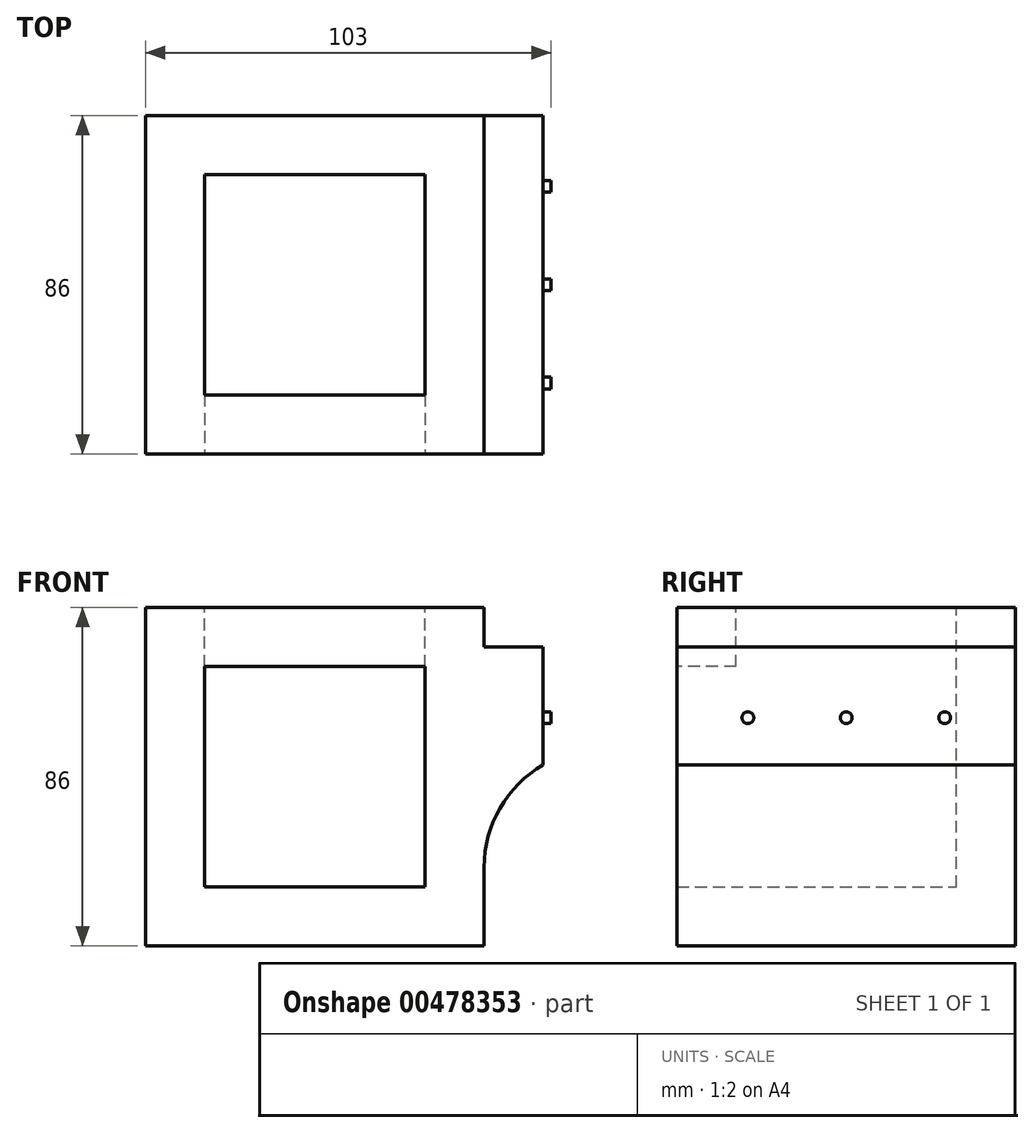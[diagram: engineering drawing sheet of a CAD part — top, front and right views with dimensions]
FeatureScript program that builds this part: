
annotation { "Feature Type Name" : "Feature", "Feature Type Description" : "" }
export const myFeature = defineFeature(function(context is Context, id is Id, definition is map)
    precondition{}
    {
        {
            var Q0;
            Q0=qCreatedBy(makeId("Top.planeOp"),FACE);
            var sketch = newSketch(context, id + "F0", { "sketchPlane" : qUnion([Q0])});
            skLineSegment(sketch, "E0", {"start": v(0, 0) * mm, "end": v(-43, 0) * mm});
            skLineSegment(sketch, "E1", {"start": v(-43, 0) * mm, "end": v(-43, 43) * mm});
            skLineSegment(sketch, "E2", {"start": v(-43, 43) * mm, "end": v(0, 43) * mm});
            skLineSegment(sketch, "E3", {"start": v(0, 43) * mm, "end": v(0, 0) * mm});
            skLineSegment(sketch, "E4.MirrorCS", {"start": v(43, 0) * mm, "end": v(43, 43) * mm});
            skLineSegment(sketch, "E5.MirrorCS", {"start": v(43, 43) * mm, "end": v(0, 43) * mm});
            skLineSegment(sketch, "E6.MirrorCS", {"start": v(43, -43) * mm, "end": v(0, -43) * mm});
            skLineSegment(sketch, "E7.MirrorCS", {"start": v(-43, -43) * mm, "end": v(0, -43) * mm});
            skLineSegment(sketch, "E8.MirrorCS", {"start": v(-43, 0) * mm, "end": v(-43, -43) * mm});
            skLineSegment(sketch, "E9.MirrorCS", {"start": v(43, 0) * mm, "end": v(43, -43) * mm});
            skSolve(sketch);
        }
        {
            var Q0;
            Q0 = qSketchRegion(id + "F0", true);
            var Q1;
            Q1=makeQuery(id+"F0.imprint","IMPRINT",FACE,{"disambiguationData":[TD([[makeQuery(id+"F0.imprint","IMPRINT",EDGE,{"derivedFrom":sQuery(id+"F0.wireOp",EDGE,"E0")}),-1.0]])]});
            extrude(context, id + "F1", {"entities" : qUnion([Q0, Q1]), "depth" : 43 * mm, "hasSecondDirection" : true, "secondDirectionOppositeDirection" : true, "secondDirectionDepth" : 43 * mm});
        }
        {
            var Q0;
            Q0=makeQuery(id+"F1.opExtrude","CAP_FACE",FACE,{"disambiguationData":[OSD([sQuery(id+"F0.wireOp",EDGE,"E1"),sQuery(id+"F0.wireOp",EDGE,"E2"),sQuery(id+"F0.wireOp",EDGE,"E4.MirrorCS"),sQuery(id+"F0.wireOp",EDGE,"E5.MirrorCS"),sQuery(id+"F0.wireOp",EDGE,"E6.MirrorCS"),sQuery(id+"F0.wireOp",EDGE,"E7.MirrorCS"),sQuery(id+"F0.wireOp",EDGE,"E8.MirrorCS"),sQuery(id+"F0.wireOp",EDGE,"E9.MirrorCS")])],"isStart":false});
            var sketch = newSketch(context, id + "F2", { "sketchPlane" : qUnion([Q0])});
            skLineSegment(sketch, "E10", {"start": v(0, 0) * mm, "end": v(0, 28) * mm});
            skLineSegment(sketch, "E11.bottom", {"start": v(0, 0) * mm, "end": v(-28, 0) * mm});
            skLineSegment(sketch, "E11.top", {"start": v(0, 28) * mm, "end": v(-28, 28) * mm});
            skLineSegment(sketch, "E11.right", {"start": v(-28, 0) * mm, "end": v(-28, 28) * mm});
            skLineSegment(sketch, "E12.MirrorCS", {"start": v(0, -28) * mm, "end": v(-28, -28) * mm});
            skLineSegment(sketch, "E13.MirrorCS", {"start": v(-28, 0) * mm, "end": v(-28, -28) * mm});
            skLineSegment(sketch, "E14.MirrorCS", {"start": v(28, 0) * mm, "end": v(28, 28) * mm});
            skLineSegment(sketch, "E15.MirrorCS", {"start": v(0, 28) * mm, "end": v(28, 28) * mm});
            skLineSegment(sketch, "E16.MirrorCS", {"start": v(0, -28) * mm, "end": v(28, -28) * mm});
            skLineSegment(sketch, "E17.MirrorCS", {"start": v(28, 0) * mm, "end": v(28, -28) * mm});
            skSolve(sketch);
        }
        {
            var Q0;
            Q0=makeQuery(id+"F2.imprint","IMPRINT",FACE,{"disambiguationData":[TD([[makeQuery(id+"F2.imprint","IMPRINT",EDGE,{"derivedFrom":sQuery(id+"F2.wireOp",EDGE,"E11.bottom")}),-1.0]])]});
            var Q1;
            Q1=makeQuery(id+"F2.imprint","IMPRINT",FACE,{"disambiguationData":[TD([[makeQuery(id+"F2.imprint","IMPRINT",EDGE,{"derivedFrom":sQuery(id+"F2.wireOp",EDGE,"E11.bottom")}),1.0]])]});
            extrude(context, id + "F3", {"entities" : qUnion([Q0, Q1]), "operationType" : NewBodyOperationType.REMOVE, "oppositeDirection" : true, "depth" : 71 * mm});
        }
        {
            var Q0;
            Q0=makeQuery(id+"F1.opExtrude","SWEPT_FACE",FACE,{"disambiguationData":[OSD([sQuery(id+"F0.wireOp",EDGE,"E6.MirrorCS"),sQuery(id+"F0.wireOp",EDGE,"E7.MirrorCS")])]});
            var sketch = newSketch(context, id + "F4", { "sketchPlane" : qUnion([Q0])});
            skLineSegment(sketch, "E18.bottom", {"start": v(0, 0) * mm, "end": v(-28, 0) * mm});
            skLineSegment(sketch, "E18.top", {"start": v(0, 28) * mm, "end": v(-28, 28) * mm});
            skLineSegment(sketch, "E18.left", {"start": v(0, 0) * mm, "end": v(0, 28) * mm});
            skLineSegment(sketch, "E18.right", {"start": v(-28, 0) * mm, "end": v(-28, 28) * mm});
            skLineSegment(sketch, "E19.MirrorCS", {"start": v(0, 28) * mm, "end": v(28, 28) * mm});
            skLineSegment(sketch, "E20.MirrorCS", {"start": v(28, 0) * mm, "end": v(28, 28) * mm});
            skLineSegment(sketch, "E21.MirrorCS", {"start": v(0, -28) * mm, "end": v(-28, -28) * mm});
            skLineSegment(sketch, "E22.MirrorCS", {"start": v(0, -28) * mm, "end": v(28, -28) * mm});
            skLineSegment(sketch, "E23.MirrorCS", {"start": v(-28, 0) * mm, "end": v(-28, -28) * mm});
            skLineSegment(sketch, "E24.MirrorCS", {"start": v(28, 0) * mm, "end": v(28, -28) * mm});
            skSolve(sketch);
        }
        {
            var Q0;
            Q0=makeQuery(id+"F4.imprint","IMPRINT",FACE,{"disambiguationData":[TD([[makeQuery(id+"F4.imprint","IMPRINT",EDGE,{"derivedFrom":sQuery(id+"F4.wireOp",EDGE,"E18.bottom")}),-1.0]])]});
            var Q1;
            Q1=makeQuery(id+"F4.imprint","IMPRINT",FACE,{"disambiguationData":[TD([[makeQuery(id+"F4.imprint","IMPRINT",EDGE,{"derivedFrom":sQuery(id+"F4.wireOp",EDGE,"E18.bottom")}),1.0]])]});
            extrude(context, id + "F5", {"entities" : qUnion([Q0, Q1]), "operationType" : NewBodyOperationType.REMOVE, "oppositeDirection" : true, "depth" : 71 * mm});
        }
        {
            var Q0;
            Q0=makeQuery(id+"F1.opExtrude","SWEPT_FACE",FACE,{"disambiguationData":[OSD([sQuery(id+"F0.wireOp",EDGE,"E4.MirrorCS"),sQuery(id+"F0.wireOp",EDGE,"E9.MirrorCS")])]});
            var sketch = newSketch(context, id + "F6", { "sketchPlane" : qUnion([Q0])});
            skLineSegment(sketch, "E25", {"start": v(0, 0) * mm, "end": v(0, 33) * mm});
            skPoint(sketch, "E25.endSnap0", {"position": v(0, 43) * mm});
            skLineSegment(sketch, "E26", {"start": v(0, 33) * mm, "end": v(43, 33) * mm});
            skLineSegment(sketch, "E27", {"start": v(43, 33) * mm, "end": v(-43, 33) * mm});
            skLineSegment(sketch, "E28", {"start": v(0, 0) * mm, "end": v(0, -23) * mm});
            skPoint(sketch, "E28.endSnap0", {"position": v(0, -43) * mm});
            skLineSegment(sketch, "E29", {"start": v(0, -23) * mm, "end": v(43, -23) * mm});
            skLineSegment(sketch, "E30", {"start": v(43, -23) * mm, "end": v(-43, -23) * mm});
            skSolve(sketch);
        }
        {
            var Q0;
            Q0 = qSketchRegion(id + "F6", true);
            var Q1;
            {var subQ2=sQuery(id+"F6.wireOp",EDGE,"E25");Q1=makeQuery(id+"F6.imprint","IMPRINT",FACE,{"disambiguationData":[TD([[makeQuery(id+"F6.imprint","IMPRINT",EDGE,{"derivedFrom":subQ2}),1.0]])]});}
            var Q2;
            {var subQ5=sQuery(id+"F6.wireOp",EDGE,"E25");Q2=makeQuery(id+"F6.imprint","IMPRINT",FACE,{"disambiguationData":[TD([[makeQuery(id+"F6.imprint","IMPRINT",EDGE,{"derivedFrom":subQ5}),-1.0]])]});}
            extrude(context, id + "F7", {"entities" : qUnion([Q0, Q1, Q2]), "operationType" : NewBodyOperationType.ADD, "depth" : 15 * mm});
        }
        {
            var Q0;
            {var subQ0=sQuery(id+"F0.wireOp",EDGE,"E6.MirrorCS");Q0=makeQuery(id+"F7.boolean.opBoolean","MERGE",FACE,{"derivedFrom":[makeQuery(id+"F1.opExtrude","SWEPT_FACE",FACE,{"disambiguationData":[OSD([subQ0,sQuery(id+"F0.wireOp",EDGE,"E7.MirrorCS")])]}),makeQuery(id+"F7.opExtrude","SWEPT_FACE",FACE,{"disambiguationData":[OSD([subQ0,sQuery(id+"F0.wireOp",EDGE,"E9.MirrorCS")])]})]});}
            var sketch = newSketch(context, id + "F8", { "sketchPlane" : qUnion([Q0])});
            skLineSegment(sketch, "E31", {"start": v(43, -43) * mm, "end": v(68, -43) * mm});
            skLineSegment(sketch, "E32", {"start": v(68, -43) * mm, "end": v(68, 7) * mm});
            skLineSegment(sketch, "E33", {"start": v(73, 7) * mm, "end": v(68, 7) * mm});
            skLineSegment(sketch, "E34", {"start": v(43, -23) * mm, "end": v(43, -43) * mm});
            skPoint(sketch, "E35.visualSharp", {"position": v(43, 7) * mm});
            skArc(sketch, "E35.filletArc", {"start": v(73, 7) * mm, "mid": v(51.79, -1.79) * mm, "end": v(43, -23) * mm});
            skSolve(sketch);
        }
        {
            var Q0;
            {var subQ0=sQuery(id+"F8.wireOp",EDGE,"E33");Q0=makeQuery(id+"F8.imprint","IMPRINT",FACE,{"disambiguationData":[TD([[makeQuery(id+"F8.imprint","IMPRINT",EDGE,{"derivedFrom":subQ0}),1.0]])]});}
            var Q1;
            {var subQ1=sQuery(id+"F0.wireOp",EDGE,"E9.MirrorCS");var subQ2=sQuery(id+"F0.wireOp",EDGE,"E6.MirrorCS");var subQ3=makeQuery(id+"F7.opExtrude","SWEPT_EDGE",EDGE,{"disambiguationData":[OSD([subQ2,subQ1,sQuery(id+"F6.wireOp",EDGE,"E30")])]});Q1=makeQuery(id+"F8.imprint","IMPRINT",FACE,{"disambiguationData":[TD([[makeQuery(id+"F8.imprint","IMPRINT",EDGE,{"derivedFrom":subQ3}),-1.0]])]});}
            extrude(context, id + "F9", {"entities" : qUnion([Q0, Q1]), "operationType" : NewBodyOperationType.REMOVE, "oppositeDirection" : true, "depth" : 100 * mm});
        }
        {
            var Q0;
            Q0=makeQuery(id+"F7.opExtrude","CAP_FACE",FACE,{"disambiguationData":[OSD([sQuery(id+"F0.wireOp",EDGE,"E4.MirrorCS"),sQuery(id+"F0.wireOp",EDGE,"E5.MirrorCS"),sQuery(id+"F0.wireOp",EDGE,"E6.MirrorCS"),sQuery(id+"F0.wireOp",EDGE,"E9.MirrorCS"),sQuery(id+"F6.wireOp",EDGE,"E27"),sQuery(id+"F6.wireOp",EDGE,"E30")])],"isStart":false});
            var sketch = newSketch(context, id + "F10", { "sketchPlane" : qUnion([Q0])});
            skLineSegment(sketch, "E36", {"start": v(0, 0) * mm, "end": v(0, 15) * mm});
            skPoint(sketch, "E36.endSnap0", {"position": v(0, 33) * mm});
            skLineSegment(sketch, "E37", {"start": v(0, 15) * mm, "end": v(-25, 15) * mm});
            skLineSegment(sketch, "E38.MirrorCS", {"start": v(0, 15) * mm, "end": v(25, 15) * mm});
            skCircle(sketch, "E39", {"center": v(-25, 15) * mm, "radius": 1.5 * mm});
            skCircle(sketch, "E40", {"center": v(25, 15) * mm, "radius": 1.5 * mm});
            skCircle(sketch, "E41", {"center": v(0, 15) * mm, "radius": 1.5 * mm});
            skSolve(sketch);
        }
        {
            var Q0;
            {var subQ1=sQuery(id+"F10.wireOp",EDGE,"E36");var subQ3=sQuery(id+"F10.wireOp",EDGE,"E41");var subQ4=makeQuery(id+"F10.imprint","INTERSECT",VERTEX,{"derivedFrom":[subQ1,subQ3]});Q0=makeQuery(id+"F10.imprint","IMPRINT",FACE,{"disambiguationData":[TD([[makeQuery(id+"F10.imprint","IMPRINT",EDGE,{"disambiguationData":[TD([[subQ4,1.0]])],"derivedFrom":subQ3}),1.0]])]});}
            var Q1;
            {var subQ1=sQuery(id+"F10.wireOp",EDGE,"E37");var subQ3=sQuery(id+"F10.wireOp",EDGE,"E41");var subQ4=makeQuery(id+"F10.imprint","INTERSECT",VERTEX,{"derivedFrom":[subQ1,subQ3]});Q1=makeQuery(id+"F10.imprint","IMPRINT",FACE,{"disambiguationData":[TD([[makeQuery(id+"F10.imprint","IMPRINT",EDGE,{"disambiguationData":[TD([[subQ4,1.0]])],"derivedFrom":subQ3}),1.0]])]});}
            var Q2;
            {var subQ1=sQuery(id+"F10.wireOp",EDGE,"E36");var subQ3=sQuery(id+"F10.wireOp",EDGE,"E41");var subQ4=makeQuery(id+"F10.imprint","INTERSECT",VERTEX,{"derivedFrom":[subQ1,subQ3]});Q2=makeQuery(id+"F10.imprint","IMPRINT",FACE,{"disambiguationData":[TD([[makeQuery(id+"F10.imprint","IMPRINT",EDGE,{"disambiguationData":[TD([[subQ4,-1.0]])],"derivedFrom":subQ3}),1.0]])]});}
            var Q3;
            Q3=makeQuery(id+"F10.imprint","IMPRINT",FACE,{"disambiguationData":[TD([[makeQuery(id+"F10.imprint","IMPRINT",EDGE,{"derivedFrom":sQuery(id+"F10.wireOp",EDGE,"E39")}),1.0]])]});
            var Q4;
            Q4=makeQuery(id+"F10.imprint","IMPRINT",FACE,{"disambiguationData":[TD([[makeQuery(id+"F10.imprint","IMPRINT",EDGE,{"derivedFrom":sQuery(id+"F10.wireOp",EDGE,"E40")}),1.0]])]});
            extrude(context, id + "F11", {"entities" : qUnion([Q0, Q1, Q2, Q3, Q4]), "operationType" : NewBodyOperationType.ADD, "depth" : 2 * mm});
        }
    });
